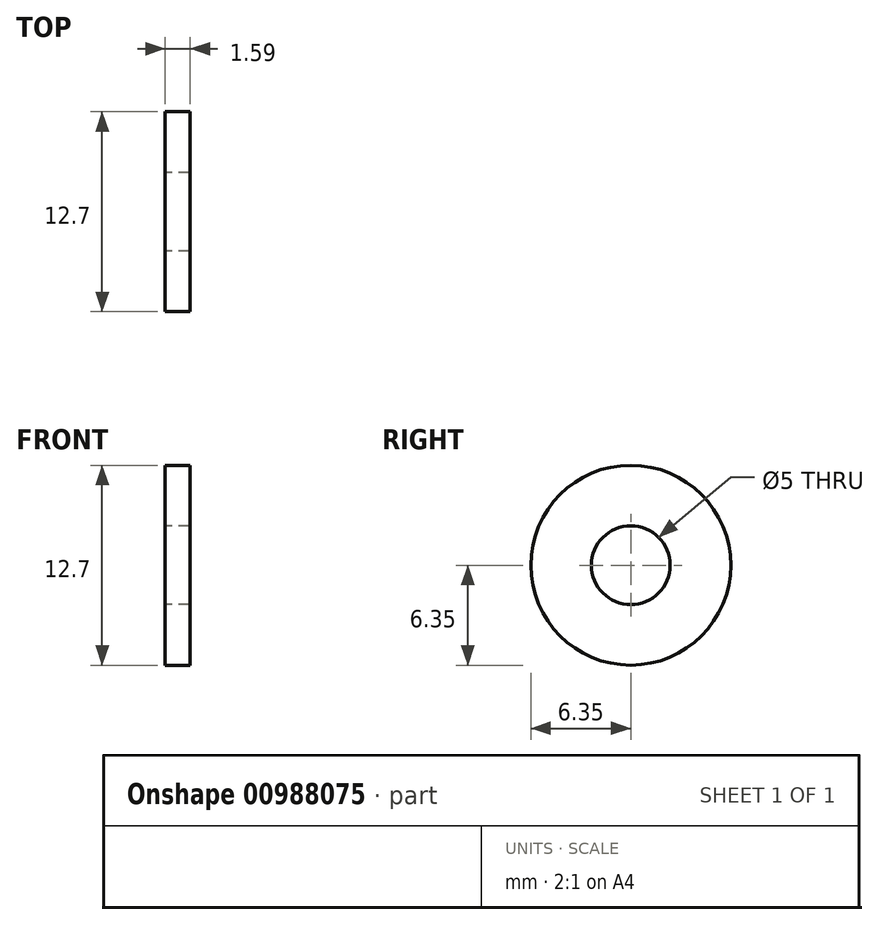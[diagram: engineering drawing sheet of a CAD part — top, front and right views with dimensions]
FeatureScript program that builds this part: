
annotation { "Feature Type Name" : "Feature", "Feature Type Description" : "" }
export const myFeature = defineFeature(function(context is Context, id is Id, definition is map)
    precondition{}
    {
        {
            var Q0;
            Q0=qCreatedBy(makeId("Right.planeOp"),FACE);
            var sketch = newSketch(context, id + "F0", { "sketchPlane" : qUnion([Q0])});
            skCircle(sketch, "E0", {"center": v(0, 0) * mm, "radius": 6.35 * mm});
            skLineSegment(sketch, "E1.bottom", {"start": v(6.35, -6.35) * mm, "end": v(-6.35, -6.35) * mm, "construction": true});
            skLineSegment(sketch, "E1.top", {"start": v(6.35, 6.35) * mm, "end": v(-6.35, 6.35) * mm, "construction": true});
            skLineSegment(sketch, "E1.left", {"start": v(6.35, -6.35) * mm, "end": v(6.35, 6.35) * mm, "construction": true});
            skLineSegment(sketch, "E1.right", {"start": v(-6.35, -6.35) * mm, "end": v(-6.35, 6.35) * mm, "construction": true});
            skPoint(sketch, "E2", {"position": v(6.35, 0) * mm});
            skPoint(sketch, "E2.positionSnap0", {"position": v(6.35, 0) * mm});
            skSolve(sketch);
        }
        {
            var Q0;
            Q0 = qSketchRegion(id + "F0", true);
            extrude(context, id + "F1", {"entities" : qUnion([Q0]), "depth" : 1.59 * mm, "offsetDistance" : 25.4 * mm});
        }
        {
            var Q0;
            Q0=sQuery(id+"F0.wireOp",VERTEX,"E0.center");
            var Q1;
            Q1=makeQuery(id+"F1.opExtrude","SWEPT_BODY",BODY,{"disambiguationData":[OSD([sQuery(id+"F0.wireOp",EDGE,"E0")])]});
            hole(context, id + "F2", {"style" : HoleStyle.SIMPLE, "endStyle" : HoleEndStyle.BLIND, "oppositeDirection" : true, "holeDiameter" : 5 * mm, "majorDiameter" : 6.35 * mm, "holeDepth" : 15 * mm, "isTappedThrough" : true, "tappedDepth" : 13.5 * mm, "tapClearance" : 3, "startFromSketch" : true, "locations" : qUnion([Q0]), "scope" : qUnion([Q1])});
        }
    });
